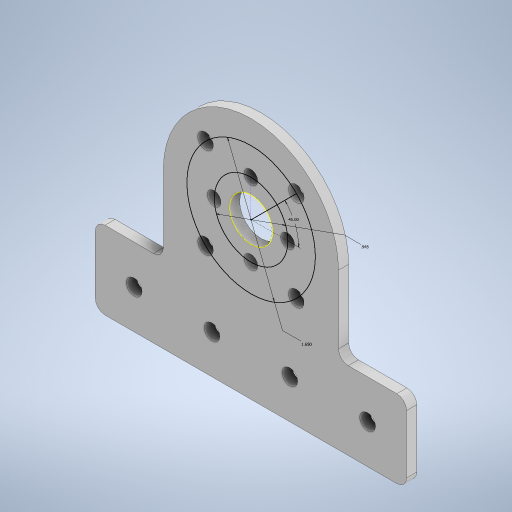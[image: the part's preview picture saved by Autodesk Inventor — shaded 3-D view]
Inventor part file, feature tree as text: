
AUTODESK INVENTOR PART (.ipt)
format: ipt  version: 2024 (Build 280153000, 153)  size: 308,736 bytes
history: native  units: in
note: dims shown in document units (in); Inventor stores cm internally (conversion verified against a paired STEP export)
features: sketch x2, hole x2, pattern_circular x2, extrude x1, fillet x1
ambient origin geometry x8: Origin, YZ Plane, XZ Plane, XY Plane, X Axis, Y Axis, Z Axis, Center Point
bodies: Solid1 (feature_tree)
feature tree (8):
  extrude  "Extrusion1"  Depth=0.13in TaperAngle=0.0deg
  fillet  "Fillet1"  Radius=0.203in
  sketch  "Sketch2"  dims[d11=0.203in d12=0.5in d13=0.5in d14=0.5in d15=0.5in d16=2.0in d17=1.0in d18=4.0in d19=2.0in d20=1.0in d21=1.0in d22=0.125in d25=1.125in d26=1.0in d27=0.9449in d28=1.65in d29=45.0deg d30=0.201in d31=0.75in d32=0.385in d33=0.25in d34=0.5635in d35=0.64in d36=0.8108in d37=1.5748in d38=360.0deg d41=0.177in d42=0.75in d43=0.375in d44=0.25in d45=0.5635in d46=0.64in d47=0.8108in d48=1.5748in d49=360.0deg]
  hole  "Hole1"  [1 undecoded]
  pattern_circular  "Circular Pattern1"  [2 undecoded]
  hole  "Hole2"  [1 undecoded]
  pattern_circular  "Circular Pattern2"  [2 undecoded]
  sketch  "Sketch1"  dims[d1=0.5512in d8=0.13in d9=0.0in d10=0.203in]
note: 6 required parameter values undecoded (feature->parameter linkage not recoverable at this tier; creation-order binding heuristic only, values carry confidence <= 0.55)
